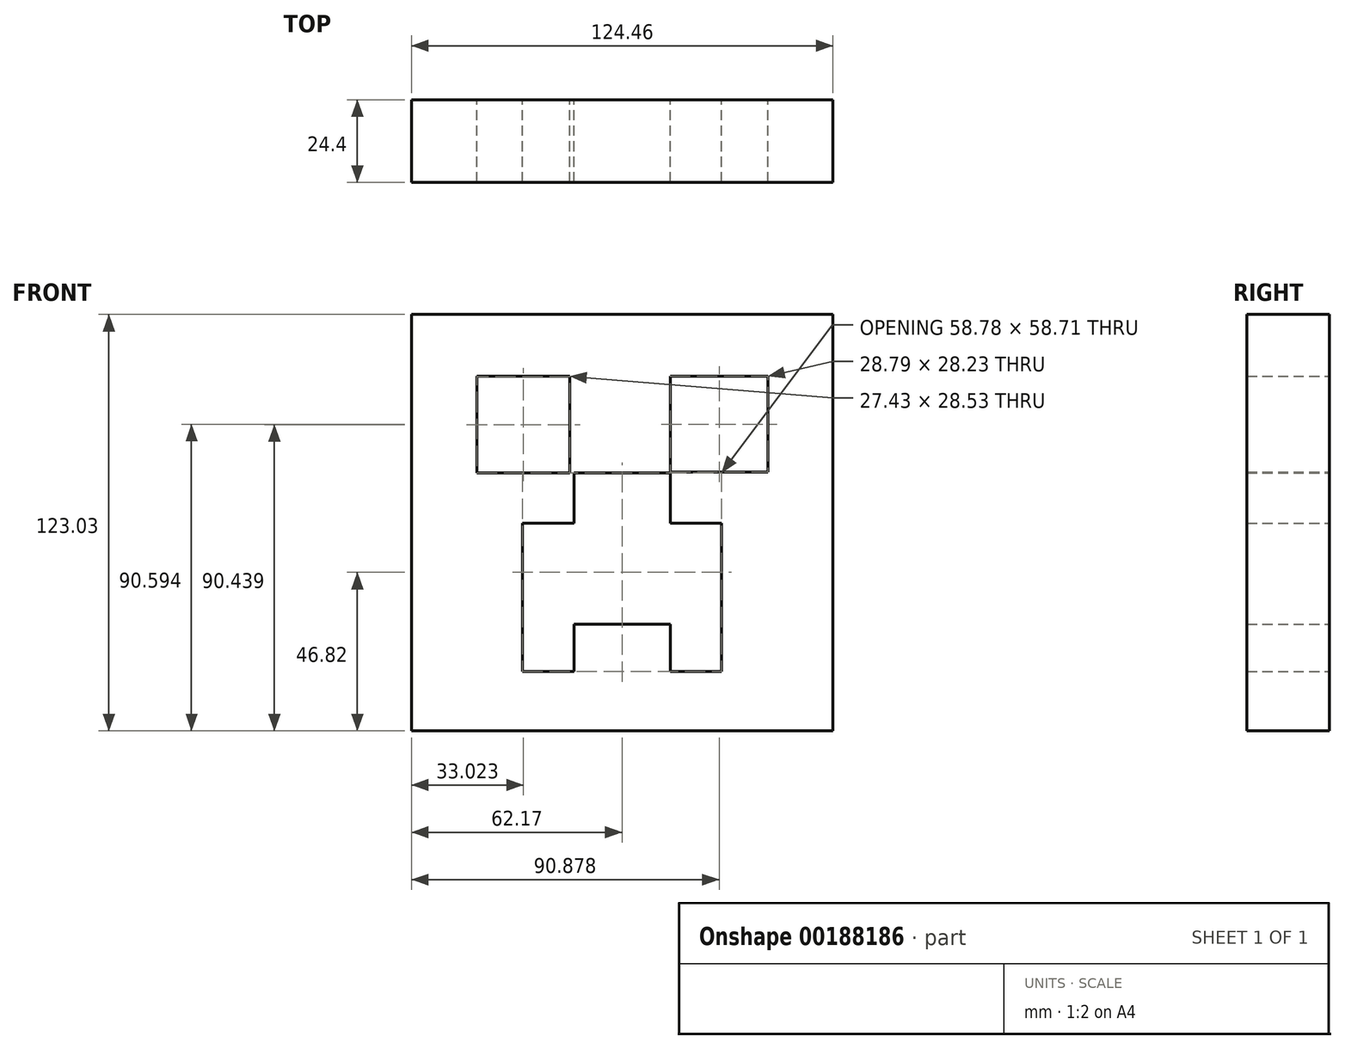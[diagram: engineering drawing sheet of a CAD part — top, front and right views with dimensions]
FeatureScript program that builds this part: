
annotation { "Feature Type Name" : "Feature", "Feature Type Description" : "" }
export const myFeature = defineFeature(function(context is Context, id is Id, definition is map)
    precondition{}
    {
        {
            var Q0;
            Q0=qCreatedBy(makeId("Front.planeOp"),FACE);
            var sketch = newSketch(context, id + "F0", { "sketchPlane" : qUnion([Q0])});
            skLineSegment(sketch, "E0.bottom", {"start": v(62.23, 63.68) * mm, "end": v(-62.23, 63.68) * mm});
            skLineSegment(sketch, "E0.top", {"start": v(62.23, -59.35) * mm, "end": v(-62.23, -59.35) * mm});
            skLineSegment(sketch, "E0.left", {"start": v(62.23, 63.68) * mm, "end": v(62.23, -59.35) * mm});
            skLineSegment(sketch, "E0.right", {"start": v(-62.23, 63.68) * mm, "end": v(-62.23, -59.35) * mm});
            skPoint(sketch, "E0.middle", {"position": v(0, 2.16) * mm});
            skSolve(sketch);
        }
        {
            var Q0;
            Q0=qCreatedBy(makeId("Front.planeOp"),FACE);
            var sketch = newSketch(context, id + "F1", { "sketchPlane" : qUnion([Q0])});
            skLineSegment(sketch, "E1.bottom", {"start": v(-15.5, 45.35) * mm, "end": v(-42.92, 45.35) * mm});
            skLineSegment(sketch, "E1.top", {"start": v(-15.5, 16.82) * mm, "end": v(-42.92, 16.82) * mm});
            skLineSegment(sketch, "E1.left", {"start": v(-15.5, 45.35) * mm, "end": v(-15.5, 16.82) * mm});
            skLineSegment(sketch, "E1.right", {"start": v(-42.92, 45.35) * mm, "end": v(-42.92, 16.82) * mm});
            skPoint(sketch, "E1.middle", {"position": v(-29.2, 31.09) * mm});
            skLineSegment(sketch, "E2.bottom", {"start": v(43.05, 45.36) * mm, "end": v(14.25, 45.36) * mm});
            skLineSegment(sketch, "E2.top", {"start": v(43.05, 17.13) * mm, "end": v(14.25, 17.13) * mm});
            skLineSegment(sketch, "E2.left", {"start": v(43.05, 45.36) * mm, "end": v(43.05, 17.13) * mm});
            skLineSegment(sketch, "E2.right", {"start": v(14.25, 45.36) * mm, "end": v(14.25, 17.13) * mm});
            skPoint(sketch, "E2.middle", {"position": v(28.65, 31.24) * mm});
            skLineSegment(sketch, "E3", {"start": v(-29.45, -41.44) * mm, "end": v(-29.45, 2.01) * mm});
            skLineSegment(sketch, "E4", {"start": v(-29.45, 2.01) * mm, "end": v(-14.28, 2.01) * mm});
            skLineSegment(sketch, "E5", {"start": v(-14.28, 2.01) * mm, "end": v(-14.28, 16.82) * mm});
            skLineSegment(sketch, "E6", {"start": v(-14.28, 16.82) * mm, "end": v(14.25, 16.82) * mm});
            skLineSegment(sketch, "E7", {"start": v(14.25, 16.82) * mm, "end": v(14.25, 2.01) * mm});
            skLineSegment(sketch, "E8", {"start": v(14.25, 2.01) * mm, "end": v(29.33, 2.01) * mm});
            skLineSegment(sketch, "E9", {"start": v(29.33, 2.01) * mm, "end": v(29.33, -41.88) * mm});
            skLineSegment(sketch, "E10", {"start": v(29.33, -41.88) * mm, "end": v(14.25, -41.88) * mm});
            skLineSegment(sketch, "E11", {"start": v(14.25, -41.88) * mm, "end": v(14.25, -27.92) * mm});
            skLineSegment(sketch, "E12", {"start": v(14.25, -27.92) * mm, "end": v(-14.28, -27.92) * mm});
            skLineSegment(sketch, "E13", {"start": v(-14.28, -27.92) * mm, "end": v(-14.28, -41.88) * mm});
            skLineSegment(sketch, "E14", {"start": v(-14.28, -41.88) * mm, "end": v(-29.45, -41.88) * mm});
            skLineSegment(sketch, "E15", {"start": v(-29.45, -41.88) * mm, "end": v(-29.45, -41.44) * mm});
            skSolve(sketch);
        }
        {
            var Q0;
            Q0 = qSketchRegion(id + "F0", true);
            extrude(context, id + "F2", {"entities" : qUnion([Q0]), "depth" : 24.4 * mm});
        }
        {
            var Q0;
            Q0 = qSketchRegion(id + "F1", true);
            extrude(context, id + "F3", {"entities" : qUnion([Q0]), "operationType" : NewBodyOperationType.REMOVE, "depth" : 25 * mm});
        }
    });
